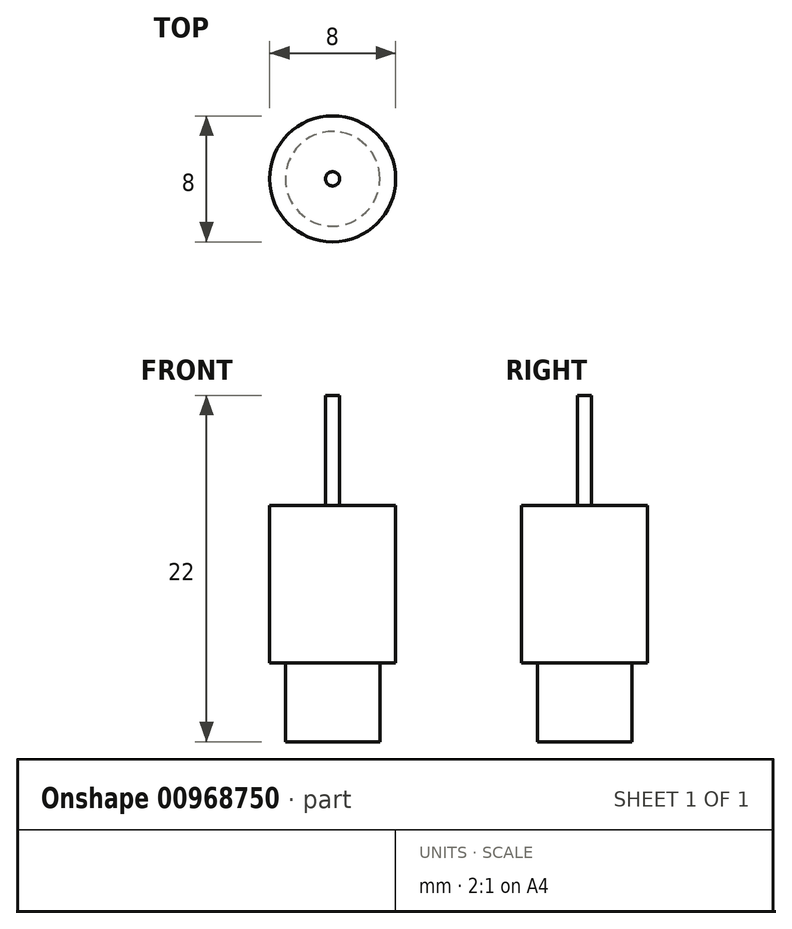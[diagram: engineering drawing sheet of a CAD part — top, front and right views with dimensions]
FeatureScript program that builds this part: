
annotation { "Feature Type Name" : "Feature", "Feature Type Description" : "" }
export const myFeature = defineFeature(function(context is Context, id is Id, definition is map)
    precondition{}
    {
        {
            var Q0;
            Q0=qCreatedBy(makeId("Front.planeOp"),FACE);
            var sketch = newSketch(context, id + "F0", { "sketchPlane" : qUnion([Q0])});
            skLineSegment(sketch, "E0", {"start": v(4, -17) * mm, "end": v(4, -7) * mm});
            skLineSegment(sketch, "E1", {"start": v(4, -7) * mm, "end": v(0.45, -7) * mm});
            skLineSegment(sketch, "E2", {"start": v(0.45, -7) * mm, "end": v(0.45, 0) * mm});
            skLineSegment(sketch, "E3", {"start": v(0.45, 0) * mm, "end": v(0, 0) * mm});
            skLineSegment(sketch, "E4", {"start": v(0, 0) * mm, "end": v(0, -22) * mm});
            skLineSegment(sketch, "E5", {"start": v(4, -17) * mm, "end": v(3, -17) * mm});
            skLineSegment(sketch, "E6", {"start": v(3, -17) * mm, "end": v(3, -22) * mm});
            skLineSegment(sketch, "E7", {"start": v(3, -22) * mm, "end": v(0, -22) * mm});
            skSolve(sketch);
        }
        {
            var Q0;
            Q0 = qSketchRegion(id + "F0", true);
            var Q1;
            Q1=sQuery(id+"F0.wireOp",EDGE,"E4");
            revolve(context, id + "F1", {"surfaceOperationType" : NewSurfaceOperationType.NEW, "entities" : qUnion([Q0]), "axis" : qUnion([Q1]), "revolveType" : RevolveType.FULL});
        }
    });
